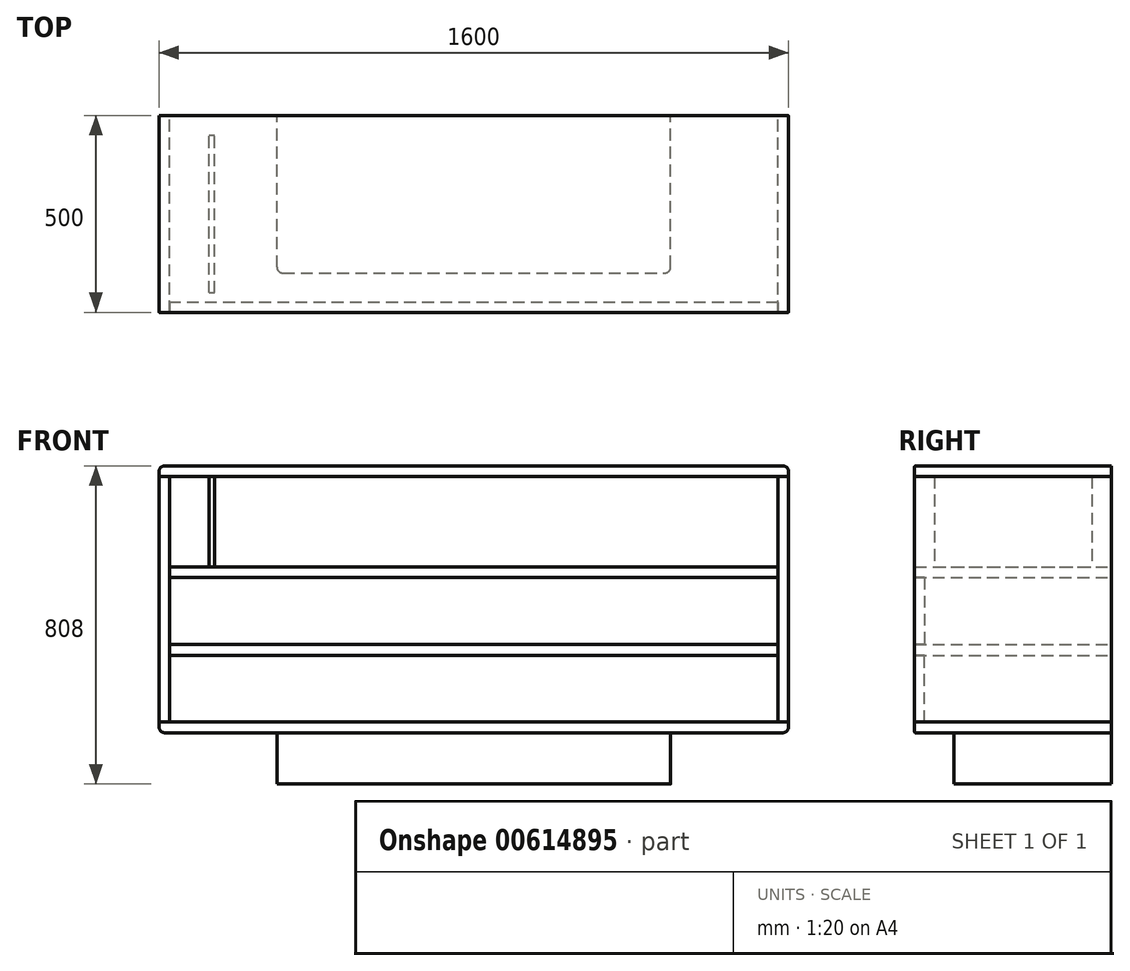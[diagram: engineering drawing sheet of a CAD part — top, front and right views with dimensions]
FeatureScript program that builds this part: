
annotation { "Feature Type Name" : "Feature", "Feature Type Description" : "" }
export const myFeature = defineFeature(function(context is Context, id is Id, definition is map)
    precondition{}
    {
        {
            var Q0;
            Q0=qCreatedBy(makeId("Front.planeOp"),FACE);
            cPlane(context, id + "F0", {"entities" : qUnion([Q0]), "cplaneType" : CPlaneType.OFFSET, "offset" : 500 * mm, "width" : 150 * mm, "height" : 150 * mm});
        }
        {
            var Q0;
            Q0=qCreatedBy(makeId("Right.planeOp"),FACE);
            cPlane(context, id + "F1", {"entities" : qUnion([Q0]), "cplaneType" : CPlaneType.OFFSET, "offset" : 800 * mm, "oppositeDirection" : true, "width" : 150 * mm, "height" : 150 * mm});
        }
        {
            var Q0;
            Q0=qCreatedBy(id+"F1.planeOp",FACE);
            cPlane(context, id + "F2", {"entities" : qUnion([Q0]), "cplaneType" : CPlaneType.OFFSET, "offset" : 27 * mm, "width" : 150 * mm, "height" : 150 * mm});
        }
        {
            var Q0;
            Q0=qCreatedBy(makeId("Top.planeOp"),FACE);
            cPlane(context, id + "F3", {"entities" : qUnion([Q0]), "cplaneType" : CPlaneType.OFFSET, "offset" : 170 * mm, "width" : 150 * mm, "height" : 150 * mm});
        }
        {
            var Q0;
            Q0=qCreatedBy(id+"F3.planeOp",FACE);
            cPlane(context, id + "F4", {"entities" : qUnion([Q0]), "cplaneType" : CPlaneType.OFFSET, "offset" : 27 * mm, "width" : 150 * mm, "height" : 150 * mm});
        }
        {
            var Q0;
            Q0=qCreatedBy(id+"F4.planeOp",FACE);
            cPlane(context, id + "F5", {"entities" : qUnion([Q0]), "cplaneType" : CPlaneType.OFFSET, "offset" : 170 * mm, "width" : 150 * mm, "height" : 150 * mm});
        }
        {
            var Q0;
            Q0=qCreatedBy(id+"F5.planeOp",FACE);
            cPlane(context, id + "F6", {"entities" : qUnion([Q0]), "cplaneType" : CPlaneType.OFFSET, "offset" : 27 * mm, "width" : 150 * mm, "height" : 150 * mm});
        }
        {
            var Q0;
            Q0=qCreatedBy(id+"F6.planeOp",FACE);
            cPlane(context, id + "F7", {"entities" : qUnion([Q0]), "cplaneType" : CPlaneType.OFFSET, "offset" : 230 * mm, "width" : 150 * mm, "height" : 150 * mm});
        }
        {
            var Q0;
            Q0=qCreatedBy(makeId("Front.planeOp"),FACE);
            var sketch = newSketch(context, id + "F8", { "sketchPlane" : qUnion([Q0])});
            skLineSegment(sketch, "E0.bottom", {"start": v(-800, 651) * mm, "end": v(0, 651) * mm});
            skLineSegment(sketch, "E0.top", {"start": v(-800, 624) * mm, "end": v(0, 624) * mm});
            skLineSegment(sketch, "E0.left", {"start": v(-800, 651) * mm, "end": v(-800, 624) * mm});
            skLineSegment(sketch, "E1.MirrorCS", {"start": v(800, 651) * mm, "end": v(0, 651) * mm});
            skLineSegment(sketch, "E2.MirrorCS", {"start": v(800, 651) * mm, "end": v(800, 624) * mm});
            skLineSegment(sketch, "E3.MirrorCS", {"start": v(800, 624) * mm, "end": v(0, 624) * mm});
            skSolve(sketch);
        }
        {
            var Q0;
            Q0=qCreatedBy(makeId("Front.planeOp"),FACE);
            var sketch = newSketch(context, id + "F9", { "sketchPlane" : qUnion([Q0])});
            skLineSegment(sketch, "E4.bottom", {"start": v(-773, 367) * mm, "end": v(0, 367) * mm});
            skLineSegment(sketch, "E4.top", {"start": v(-773, 394) * mm, "end": v(0, 394) * mm});
            skLineSegment(sketch, "E4.left", {"start": v(-773, 367) * mm, "end": v(-773, 394) * mm});
            skLineSegment(sketch, "E5.MirrorCS", {"start": v(773, 367) * mm, "end": v(0, 367) * mm});
            skLineSegment(sketch, "E6.MirrorCS", {"start": v(773, 394) * mm, "end": v(0, 394) * mm});
            skLineSegment(sketch, "E7.MirrorCS", {"start": v(773, 367) * mm, "end": v(773, 394) * mm});
            skSolve(sketch);
        }
        {
            var Q0;
            Q0=qCreatedBy(makeId("Front.planeOp"),FACE);
            var sketch = newSketch(context, id + "F10", { "sketchPlane" : qUnion([Q0])});
            skLineSegment(sketch, "E8.bottom", {"start": v(-773, 170) * mm, "end": v(0, 170) * mm});
            skLineSegment(sketch, "E8.top", {"start": v(-773, 197) * mm, "end": v(0, 197) * mm});
            skLineSegment(sketch, "E8.left", {"start": v(-773, 170) * mm, "end": v(-773, 197) * mm});
            skLineSegment(sketch, "E8.right", {"start": v(0, 170) * mm, "end": v(0, 197) * mm});
            skLineSegment(sketch, "E9.MirrorCS", {"start": v(773, 170) * mm, "end": v(0, 170) * mm});
            skLineSegment(sketch, "E10.MirrorCS", {"start": v(773, 197) * mm, "end": v(0, 197) * mm});
            skLineSegment(sketch, "E11.MirrorCS", {"start": v(773, 170) * mm, "end": v(773, 197) * mm});
            skSolve(sketch);
        }
        {
            var Q0;
            Q0=qCreatedBy(makeId("Front.planeOp"),FACE);
            var sketch = newSketch(context, id + "F11", { "sketchPlane" : qUnion([Q0])});
            skLineSegment(sketch, "E12.bottom", {"start": v(-800, -27) * mm, "end": v(0, -27) * mm});
            skLineSegment(sketch, "E12.top", {"start": v(-800, 0) * mm, "end": v(0, 0) * mm});
            skLineSegment(sketch, "E12.left", {"start": v(-800, 0) * mm, "end": v(-800, -27) * mm});
            skLineSegment(sketch, "E12.right", {"start": v(0, 0) * mm, "end": v(0, -27) * mm});
            skLineSegment(sketch, "E13.MirrorCS", {"start": v(800, -27) * mm, "end": v(0, -27) * mm});
            skLineSegment(sketch, "E14.MirrorCS", {"start": v(800, 0) * mm, "end": v(0, 0) * mm});
            skLineSegment(sketch, "E15.MirrorCS", {"start": v(800, 0) * mm, "end": v(800, -27) * mm});
            skSolve(sketch);
        }
        {
            var Q0;
            Q0=qCreatedBy(makeId("Front.planeOp"),FACE);
            var sketch = newSketch(context, id + "F12", { "sketchPlane" : qUnion([Q0])});
            skLineSegment(sketch, "E16.bottom", {"start": v(-800, 624) * mm, "end": v(-773, 624) * mm});
            skLineSegment(sketch, "E16.top", {"start": v(-800, 0) * mm, "end": v(-773, 0) * mm});
            skLineSegment(sketch, "E16.left", {"start": v(-800, 624) * mm, "end": v(-800, 0) * mm});
            skLineSegment(sketch, "E16.right", {"start": v(-773, 624) * mm, "end": v(-773, 0) * mm});
            skSolve(sketch);
        }
        {
            var Q0;
            Q0=qSketchRegion(id+"F8",true);
            var Q1;
            Q1=qSketchRegion(id+"F9",true);
            var Q2;
            Q2=qSketchRegion(id+"F10",true);
            var Q3;
            Q3=qSketchRegion(id+"F11",true);
            var Q4;
            Q4=qSketchRegion(id+"F12",true);
            var Q5;
            Q5=qCreatedBy(id+"F0.planeOp",FACE);
            extrude(context, id + "F13", {"entities" : qUnion([Q0, Q1, Q2, Q3, Q4]), "endBound" : BoundingType.UP_TO_SURFACE, "depth" : 500 * mm, "endBoundEntityFace" : qUnion([Q5]), "offsetDistance" : 25 * mm});
        }
        {
            var Q0;
            Q0=makeQuery(id+"F13.opExtrude","SWEPT_BODY",BODY,{"disambiguationData":[OSD([sQuery(id+"F12.wireOp",EDGE,"E16.bottom"),sQuery(id+"F12.wireOp",EDGE,"E16.top"),sQuery(id+"F12.wireOp",EDGE,"E16.left"),sQuery(id+"F12.wireOp",EDGE,"E16.right")])]});
            var Q1;
            Q1=qCreatedBy(makeId("Right.planeOp"),FACE);
            mirror(context, id + "F14", {"entities" : qUnion([Q0]), "mirrorPlane" : qUnion([Q1])});
        }
        {
            var Q0;
            Q0=qCreatedBy(id+"F0.planeOp",FACE);
            var sketch = newSketch(context, id + "F15", { "sketchPlane" : qUnion([Q0])});
            skLineSegment(sketch, "E17.bottom", {"start": v(773, 367) * mm, "end": v(-773, 367) * mm});
            skLineSegment(sketch, "E17.top", {"start": v(773, 197) * mm, "end": v(-773, 197) * mm});
            skLineSegment(sketch, "E17.left", {"start": v(773, 367) * mm, "end": v(773, 197) * mm});
            skLineSegment(sketch, "E17.right", {"start": v(-773, 367) * mm, "end": v(-773, 197) * mm});
            skPoint(sketch, "E17.middle", {"position": v(0, 282) * mm});
            skLineSegment(sketch, "E18.bottom", {"start": v(773, 0) * mm, "end": v(-773, 0) * mm});
            skLineSegment(sketch, "E18.top", {"start": v(773, 170) * mm, "end": v(-773, 170) * mm});
            skLineSegment(sketch, "E18.left", {"start": v(773, 0) * mm, "end": v(773, 170) * mm});
            skLineSegment(sketch, "E18.right", {"start": v(-773, 0) * mm, "end": v(-773, 170) * mm});
            skPoint(sketch, "E18.middle", {"position": v(0, 85) * mm});
            skSolve(sketch);
        }
        {
            var Q0;
            Q0=qSketchRegion(id+"F15",true);
            var Q1;
            Q1=qCreatedBy(id+"F0.planeOp",FACE);
            extrude(context, id + "F16", {"entities" : qUnion([Q0]), "oppositeDirection" : true, "depth" : 25 * mm, "endBoundEntityFace" : qUnion([Q1]), "offsetDistance" : 25 * mm});
        }
        {
            var Q0;
            Q0=makeQuery(id+"F13.opExtrude","SWEPT_EDGE",EDGE,{"disambiguationData":[OSD([sQuery(id+"F11.wireOp",EDGE,"E12.bottom"),sQuery(id+"F11.wireOp",EDGE,"E12.left")])]});
            var Q1;
            Q1=makeQuery(id+"F13.opExtrude","SWEPT_EDGE",EDGE,{"disambiguationData":[OSD([sQuery(id+"F8.wireOp",EDGE,"E0.bottom"),sQuery(id+"F8.wireOp",EDGE,"E0.left")])]});
            var Q2;
            Q2=makeQuery(id+"F13.opExtrude","SWEPT_EDGE",EDGE,{"disambiguationData":[OSD([sQuery(id+"F8.wireOp",EDGE,"E1.MirrorCS"),sQuery(id+"F8.wireOp",EDGE,"E2.MirrorCS")])]});
            var Q3;
            Q3=makeQuery(id+"F13.opExtrude","SWEPT_EDGE",EDGE,{"disambiguationData":[OSD([sQuery(id+"F11.wireOp",EDGE,"E13.MirrorCS"),sQuery(id+"F11.wireOp",EDGE,"E15.MirrorCS")])]});
            fillet(context, id + "F17", {"entities" : qUnion([Q0, Q1, Q2, Q3]), "radius" : 15 * mm, "tangentPropagation" : true, "allowEdgeOverflow" : false});
        }
        {
            var Q0;
            Q0=makeQuery(id+"F13.opExtrude","CAP_EDGE",EDGE,{"disambiguationData":[OSD([sQuery(id+"F8.wireOp",EDGE,"E0.bottom"),sQuery(id+"F8.wireOp",EDGE,"E1.MirrorCS")])],"isStart":false});
            var Q1;
            Q1=makeQuery(id+"F13.opExtrude","CAP_EDGE",EDGE,{"disambiguationData":[OSD([sQuery(id+"F12.wireOp",EDGE,"E16.left")])],"isStart":false});
            var Q2;
            Q2=makeQuery(id+"F13.opExtrude","CAP_EDGE",EDGE,{"disambiguationData":[OSD([sQuery(id+"F11.wireOp",EDGE,"E12.bottom"),sQuery(id+"F11.wireOp",EDGE,"E13.MirrorCS")])],"isStart":false});
            var Q3;
            Q3=makeQuery(id+"F14.opPattern","COPY",EDGE,{"derivedFrom":makeQuery(id+"F13.opExtrude","CAP_EDGE",EDGE,{"disambiguationData":[OSD([sQuery(id+"F12.wireOp",EDGE,"E16.left")])],"isStart":false}),"instanceName":"1"});
            fillet(context, id + "F18", {"entities" : qUnion([Q0, Q1, Q2, Q3]), "radius" : 2 * mm, "tangentPropagation" : true, "allowEdgeOverflow" : false});
        }
        {
            var Q0;
            Q0=qCreatedBy(makeId("Front.planeOp"),FACE);
            var sketch = newSketch(context, id + "F19", { "sketchPlane" : qUnion([Q0])});
            skLineSegment(sketch, "E19.bottom", {"start": v(-500, -27) * mm, "end": v(500, -27) * mm});
            skLineSegment(sketch, "E19.top", {"start": v(-500, -157) * mm, "end": v(500, -157) * mm});
            skLineSegment(sketch, "E19.left", {"start": v(-500, -27) * mm, "end": v(-500, -157) * mm});
            skLineSegment(sketch, "E19.right", {"start": v(500, -27) * mm, "end": v(500, -157) * mm});
            skSolve(sketch);
        }
        {
            var Q0;
            Q0=qSketchRegion(id+"F19",true);
            extrude(context, id + "F20", {"entities" : qUnion([Q0]), "operationType" : NewBodyOperationType.ADD, "depth" : 400 * mm, "offsetDistance" : 25 * mm});
        }
        {
            var Q0;
            Q0=qCreatedBy(makeId("Front.planeOp"),FACE);
            var sketch = newSketch(context, id + "F21", { "sketchPlane" : qUnion([Q0])});
            skLineSegment(sketch, "E20.bottom", {"start": v(-673, 624) * mm, "end": v(-658, 624) * mm});
            skLineSegment(sketch, "E20.top", {"start": v(-673, 394) * mm, "end": v(-658, 394) * mm});
            skLineSegment(sketch, "E20.left", {"start": v(-673, 624) * mm, "end": v(-673, 394) * mm});
            skLineSegment(sketch, "E20.right", {"start": v(-658, 624) * mm, "end": v(-658, 394) * mm});
            skSolve(sketch);
        }
        {
            var Q0;
            Q0=qSketchRegion(id+"F21",true);
            extrude(context, id + "F22", {"entities" : qUnion([Q0]), "depth" : 450 * mm, "offsetDistance" : 25 * mm, "hasSecondDirection" : true, "secondDirectionOppositeDirection" : true, "secondDirectionDepth" : -50 * mm});
        }
        {
            var Q0;
            Q0=makeQuery(id+"F20.opExtrude","CAP_EDGE",EDGE,{"disambiguationData":[OSD([sQuery(id+"F19.wireOp",EDGE,"E19.left")])],"isStart":false});
            var Q1;
            Q1=makeQuery(id+"F20.opExtrude","CAP_EDGE",EDGE,{"disambiguationData":[OSD([sQuery(id+"F19.wireOp",EDGE,"E19.right")])],"isStart":false});
            fillet(context, id + "F23", {"entities" : qUnion([Q0, Q1]), "radius" : 15 * mm, "tangentPropagation" : true, "allowEdgeOverflow" : false});
        }
    });
